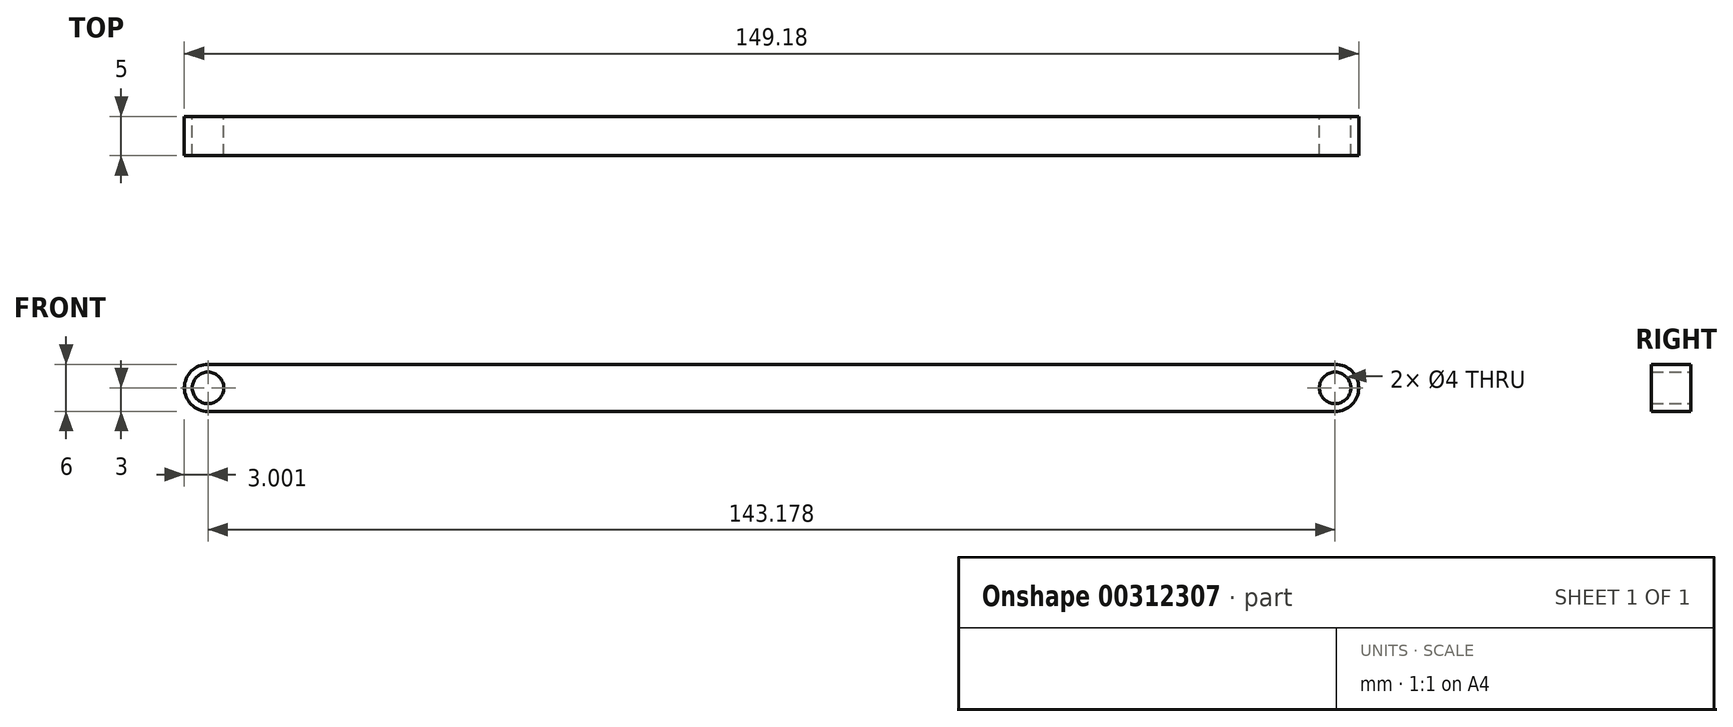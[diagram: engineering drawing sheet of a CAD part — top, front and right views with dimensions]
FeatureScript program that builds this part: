
annotation { "Feature Type Name" : "Feature", "Feature Type Description" : "" }
export const myFeature = defineFeature(function(context is Context, id is Id, definition is map)
    precondition{}
    {
        {
            var Q0;
            Q0=qCreatedBy(makeId("Front.planeOp"),FACE);
            var sketch = newSketch(context, id + "F0", { "sketchPlane" : qUnion([Q0])});
            skCircle(sketch, "E0", {"center": v(-71.59, 0) * mm, "radius": 2 * mm});
            skCircle(sketch, "E1", {"center": v(71.59, 0) * mm, "radius": 2 * mm});
            skArc(sketch, "E2", {"start": v(-71.59, 3) * mm, "mid": v(-74.59, 0) * mm, "end": v(-71.59, -3) * mm});
            skArc(sketch, "E3", {"start": v(71.59, -3) * mm, "mid": v(74.59, 0) * mm, "end": v(71.59, 3) * mm});
            skLineSegment(sketch, "E4", {"start": v(-71.59, 8.08) * mm, "end": v(-71.59, -8.9) * mm, "construction": true});
            skLineSegment(sketch, "E5", {"start": v(71.59, 8.81) * mm, "end": v(71.59, -10.37) * mm, "construction": true});
            skLineSegment(sketch, "E6", {"start": v(-71.59, 3) * mm, "end": v(71.59, 3) * mm});
            skLineSegment(sketch, "E7", {"start": v(-71.59, -3) * mm, "end": v(71.59, -3) * mm});
            skSolve(sketch);
        }
        {
            var Q0;
            Q0=makeQuery(id+"F0.imprint","IMPRINT",FACE,{"disambiguationData":[TD([[makeQuery(id+"F0.imprint","IMPRINT",EDGE,{"derivedFrom":sQuery(id+"F0.wireOp",EDGE,"E0")}),-1.0]])]});
            extrude(context, id + "F1", {"entities" : qUnion([Q0]), "depth" : 5 * mm});
        }
    });
